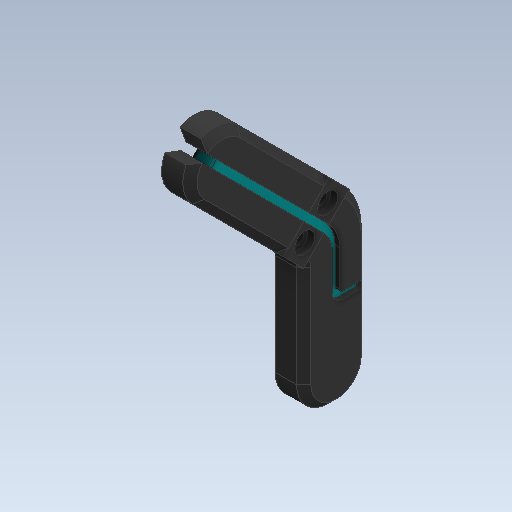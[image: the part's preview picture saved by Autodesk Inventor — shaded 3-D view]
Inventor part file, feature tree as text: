
AUTODESK INVENTOR PART (.ipt)
format: ipt  version: 2020 (Build 240168000, 168)  size: 509,952 bytes
history: native  units: in
note: dims shown in document units (in); Inventor stores cm internally (conversion verified against a paired STEP export)
features: sketch x30, other x8, projected_geometry x6, extrude x5, plane x4, chamfer x3
ambient origin geometry x8: Origin, YZ Plane, XZ Plane, XY Plane, X Axis, Y Axis, Z Axis, Center Point
bodies: Solid2 (feature_tree), Solid3 (feature_tree), Solid1 (feature_tree), Solid4 (feature_tree), Solid5 (feature_tree)
feature tree (56):
  other  "LegMidTop.ipt"
  extrude  "Extrusion3"  Depth=0.3937in
  extrude  "Extrusion4"  TaperAngle=90.0deg  [1 undecoded]
  extrude  "Extrusion5"  Depth=0.0787in
  chamfer  "Chamfer1"  Distance=0.3937in
  extrude  "Extrusion7"  Depth=0.0787in
  chamfer  "Chamfer2"  Distance=0.0984in
  chamfer  "Chamfer3"  Distance=0.0984in
  extrude  "Extrusion8"  Depth=0.0787in TaperAngle=0.0deg
  other  "Solid1::LegMidTop.ipt"
  other  "Solid2::LegMidTop.ipt"
  other  "Solid3::LegMidTop.ipt"
  other  "Solid4::LegMidTop.ipt"
  other  "Solid5::LegMidTop.ipt"
  other  "Solid6::LegMidTop.ipt"
  other  "TaggingFeature1"
  sketch  "Sketch1"  dims[d0=0.3937in d5=0.2362in]
  sketch  "Sketch2"  dims[d6=0.0394in d7=90.0deg]
  sketch  "Sketch3"  dims[d8=0.0787in d9=0.0197in]
  sketch  "Sketch4"  dims[d10=0.0394in]
  sketch  "Sketch5"  dims[d11=0.0591in d12=0.3937in d13=0.0in]
  sketch  "Sketch12"  dims[d14=0.0787in d15=0.315in]
  sketch  "Sketch14"  dims[d16=0.3937in]
  sketch  "Sketch15"  dims[d17=0.0787in]
  sketch  "Sketch16"  dims[d20=0.0in]
  sketch  "Sketch17"  dims[d21=0.315in]
  sketch  "Sketch19"  dims[d22=0.2756in]
  sketch  "Sketch22"  dims[d23=0.0787in]
  sketch  "Sketch23"  dims[d24=0.0354in]
  sketch  "Sketch24"  dims[d25=0.1142in d26=0.0984in d27=0.0in]
  sketch  "Sketch25"  dims[d28=0.0787in d29=0.0984in d30=0.0in]
  sketch  "Sketch26"  dims[d35=0.0787in d36=0.0787in d37=45.0deg d38=0.6688in d39=0.0in]
  sketch  "Sketch27"  dims[d40=0.0787in d41=0.0787in d42=45.0deg]
  sketch  "Sketch28"  dims[d43=0.0787in d44=0.0787in d45=45.0deg]
  sketch  "Sketch29"  dims[d46=0.0039in]
  sketch  "Sketch30"  dims[d47=0.3937in d48=0.0in]
  sketch  "Sketch31"  dims[d3=0.0197in]
  sketch  "Sketch32"  dims[d4=0.0344in]
  sketch  "Sketch33"
  sketch  "Sketch39"
  sketch  "Sketch40"
  plane  "Work Plane1"
  plane  "Work Plane2"
  plane  "Work Plane3"
  plane  "Work Plane4"
  sketch  "Sketch44"
  projected_geometry  "Projected Loop5"
  sketch  "Sketch45"
  projected_geometry  "Projected Loop6"
  projected_geometry  "Projected Loop7"
  sketch  "Sketch46"
  projected_geometry  "Projected Loop8"
  sketch  "Sketch48"
  projected_geometry  "Projected Loop11"
  sketch  "Sketch49"
  projected_geometry  "Projected Loop12"
note: 1 required parameter value undecoded (feature->parameter linkage not recoverable at this tier; creation-order binding heuristic only, values carry confidence <= 0.55)
